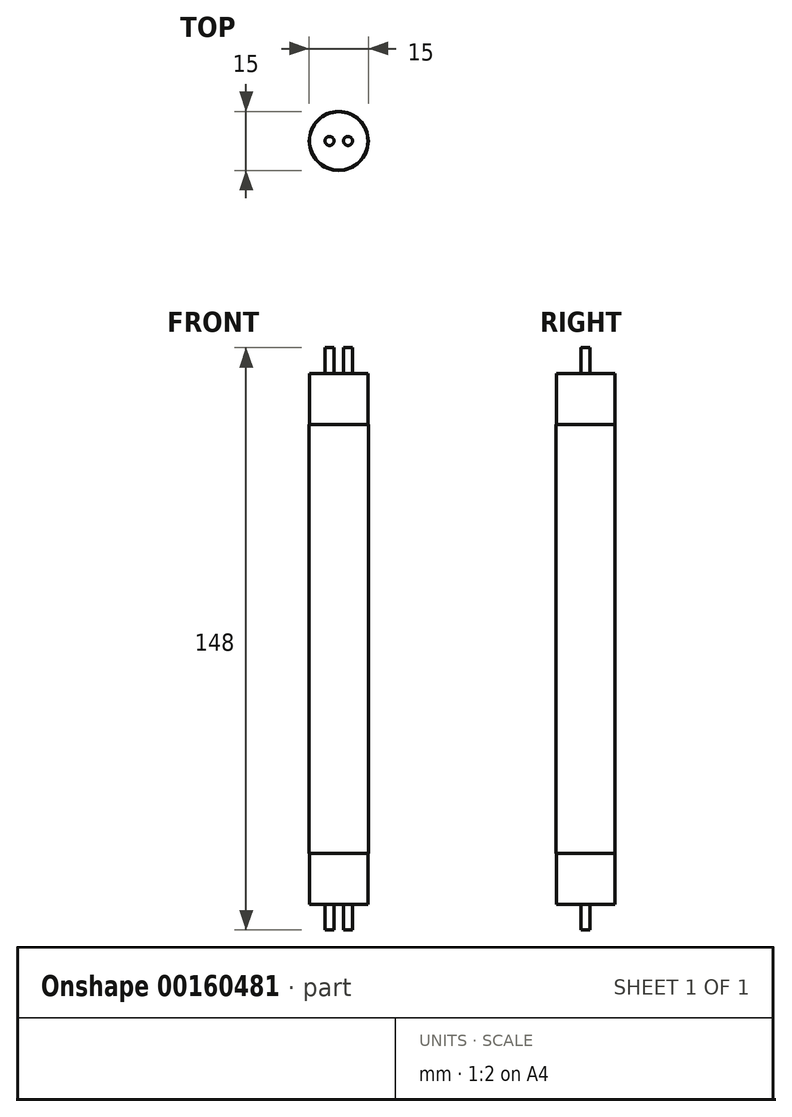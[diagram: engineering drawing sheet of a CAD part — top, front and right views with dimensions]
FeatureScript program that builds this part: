
annotation { "Feature Type Name" : "Feature", "Feature Type Description" : "" }
export const myFeature = defineFeature(function(context is Context, id is Id, definition is map)
    precondition{}
    {
        {
            var Q0;
            Q0=qCreatedBy(makeId("Top.planeOp"),FACE);
            var sketch = newSketch(context, id + "F0", { "sketchPlane" : qUnion([Q0])});
            skCircle(sketch, "E0", {"center": v(0, 0) * mm, "radius": 7.5 * mm});
            skSolve(sketch);
        }
        {
            var Q0;
            Q0 = qSketchRegion(id + "F0", true);
            extrude(context, id + "F1", {"entities" : qUnion([Q0]), "endBound" : BoundingType.SYMMETRIC, "depth" : 109 * mm});
        }
        {
            var Q0;
            Q0=makeQuery(id+"F1.opExtrude","CAP_FACE",FACE,{"disambiguationData":[OSD([sQuery(id+"F0.wireOp",EDGE,"E0")])],"isStart":false});
            var sketch = newSketch(context, id + "F2", { "sketchPlane" : qUnion([Q0])});
            skCircle(sketch, "E1", {"center": v(0, 0) * mm, "radius": 7.4 * mm});
            skSolve(sketch);
        }
        {
            var Q0;
            Q0 = qSketchRegion(id + "F2", true);
            extrude(context, id + "F3", {"entities" : qUnion([Q0]), "depth" : 12.9 * mm});
        }
        {
            var Q0;
            Q0=makeQuery(id+"F3.opExtrude","CAP_FACE",FACE,{"disambiguationData":[OSD([sQuery(id+"F2.wireOp",EDGE,"E1")])],"isStart":false});
            var sketch = newSketch(context, id + "F4", { "sketchPlane" : qUnion([Q0])});
            skLineSegment(sketch, "E2", {"start": v(-3.5, 0) * mm, "end": v(3.5, 0) * mm, "construction": true});
            skCircle(sketch, "E3", {"center": v(-2.35, 0) * mm, "radius": 1.15 * mm});
            skCircle(sketch, "E4", {"center": v(2.35, 0) * mm, "radius": 1.15 * mm});
            skPoint(sketch, "E5", {"position": v(-3.5, 0) * mm});
            skPoint(sketch, "E6", {"position": v(3.5, 0) * mm});
            skSolve(sketch);
        }
        {
            var Q0;
            Q0 = qSketchRegion(id + "F4", true);
            extrude(context, id + "F5", {"entities" : qUnion([Q0]), "operationType" : NewBodyOperationType.ADD, "depth" : 6.6 * mm});
        }
        {
            var Q0;
            Q0=makeQuery(id+"F3.opExtrude","SWEPT_BODY",BODY,{"disambiguationData":[OSD([sQuery(id+"F2.wireOp",EDGE,"E1")])]});
            var Q1;
            Q1=qCreatedBy(makeId("Top.planeOp"),FACE);
            mirror(context, id + "F6", {"entities" : qUnion([Q0]), "mirrorPlane" : qUnion([Q1])});
        }
    });
